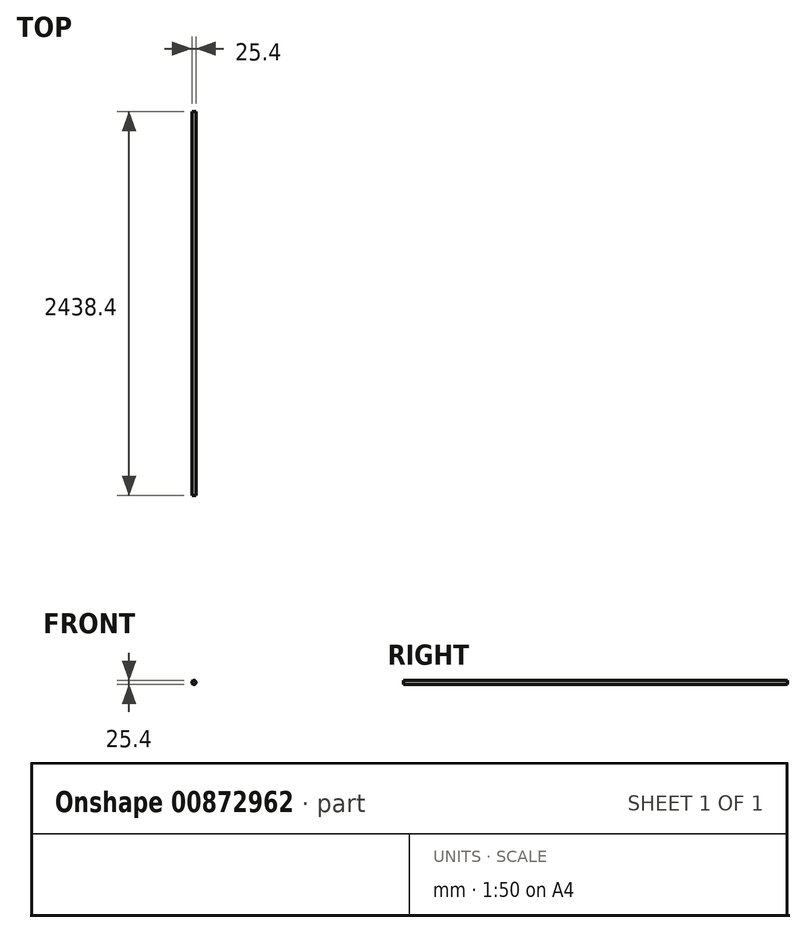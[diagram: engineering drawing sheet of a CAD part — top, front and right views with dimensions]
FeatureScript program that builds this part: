
annotation { "Feature Type Name" : "Feature", "Feature Type Description" : "" }
export const myFeature = defineFeature(function(context is Context, id is Id, definition is map)
    precondition{}
    {
        {
            var Q0;
            Q0=qCreatedBy(makeId("Front.planeOp"),FACE);
            var sketch = newSketch(context, id + "F0", { "sketchPlane" : qUnion([Q0])});
            skCircle(sketch, "E0", {"center": v(0, 0) * mm, "radius": 12.7 * mm});
            skSolve(sketch);
        }
        {
            var Q0;
            Q0 = qSketchRegion(id + "F0", true);
            extrude(context, id + "F1", {"entities" : qUnion([Q0]), "oppositeDirection" : true, "depth" : 2438.4 * mm, "offsetDistance" : 25.4 * mm});
        }
    });
